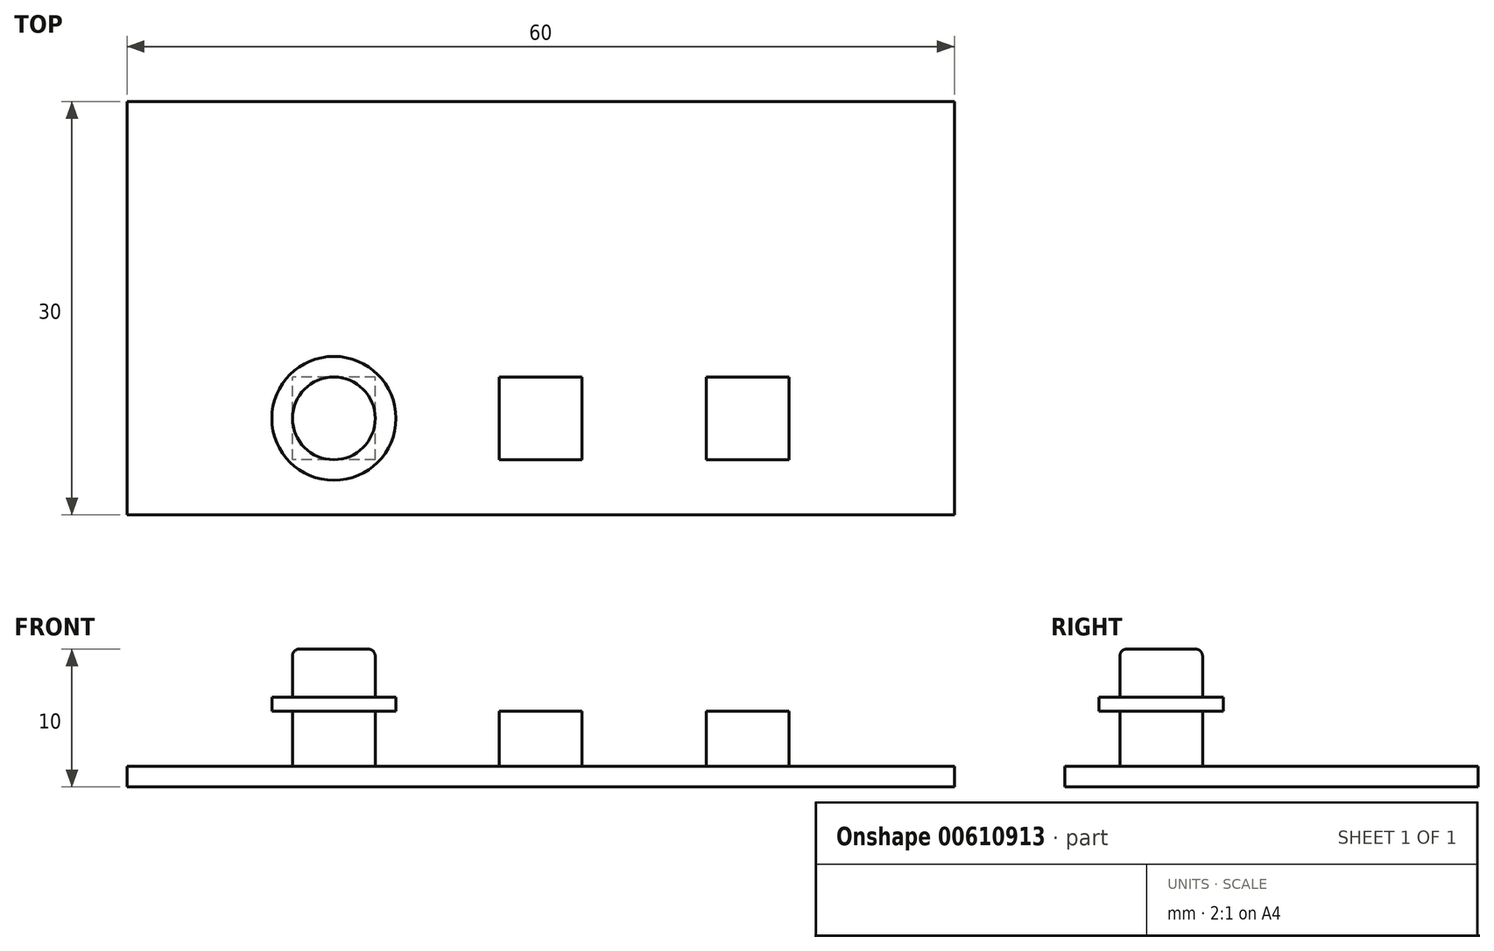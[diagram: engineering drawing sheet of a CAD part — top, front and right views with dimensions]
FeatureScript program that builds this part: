
annotation { "Feature Type Name" : "Feature", "Feature Type Description" : "" }
export const myFeature = defineFeature(function(context is Context, id is Id, definition is map)
    precondition{}
    {
        {
            var Q0;
            Q0=qCreatedBy(makeId("Top.planeOp"),FACE);
            var sketch = newSketch(context, id + "F0", { "sketchPlane" : qUnion([Q0])});
            skLineSegment(sketch, "E0.bottom", {"start": v(30, -15) * mm, "end": v(-30, -15) * mm});
            skLineSegment(sketch, "E0.top", {"start": v(30, 15) * mm, "end": v(-30, 15) * mm});
            skLineSegment(sketch, "E0.left", {"start": v(30, -15) * mm, "end": v(30, 15) * mm});
            skLineSegment(sketch, "E0.right", {"start": v(-30, -15) * mm, "end": v(-30, 15) * mm});
            skPoint(sketch, "E0.middle", {"position": v(0, 0) * mm});
            skSolve(sketch);
        }
        {
            var Q0;
            Q0=makeQuery(id+"F0.imprint","IMPRINT",FACE,{"disambiguationData":[TD([[makeQuery(id+"F0.imprint","IMPRINT",EDGE,{"derivedFrom":sQuery(id+"F0.wireOp",EDGE,"E0.bottom")}),-1.0]])]});
            extrude(context, id + "F1", {"entities" : qUnion([Q0]), "depth" : 1.5 * mm, "offsetDistance" : 25 * mm});
        }
        {
            var Q0;
            Q0=makeQuery(id+"F1.opExtrude","CAP_FACE",FACE,{"disambiguationData":[OSD([sQuery(id+"F0.wireOp",EDGE,"E0.bottom"),sQuery(id+"F0.wireOp",EDGE,"E0.top"),sQuery(id+"F0.wireOp",EDGE,"E0.left"),sQuery(id+"F0.wireOp",EDGE,"E0.right")])],"isStart":false});
            var sketch = newSketch(context, id + "F2", { "sketchPlane" : qUnion([Q0])});
            skLineSegment(sketch, "E1.bottom", {"start": v(-12, -11) * mm, "end": v(-18, -11) * mm});
            skLineSegment(sketch, "E1.top", {"start": v(-12, -5) * mm, "end": v(-18, -5) * mm});
            skLineSegment(sketch, "E1.left", {"start": v(-12, -11) * mm, "end": v(-12, -5) * mm});
            skLineSegment(sketch, "E1.right", {"start": v(-18, -11) * mm, "end": v(-18, -5) * mm});
            skPoint(sketch, "E1.middle", {"position": v(-15, -8) * mm});
            skLineSegment(sketch, "E2.1.0.0", {"start": v(3, -11) * mm, "end": v(-3, -11) * mm});
            skLineSegment(sketch, "E2.1.0.1", {"start": v(-3, -11) * mm, "end": v(-3, -5) * mm});
            skLineSegment(sketch, "E2.1.0.2", {"start": v(3, -5) * mm, "end": v(-3, -5) * mm});
            skLineSegment(sketch, "E2.1.0.3", {"start": v(3, -11) * mm, "end": v(3, -5) * mm});
            skLineSegment(sketch, "E2.2.0.0", {"start": v(18, -11) * mm, "end": v(12, -11) * mm});
            skLineSegment(sketch, "E2.2.0.1", {"start": v(12, -11) * mm, "end": v(12, -5) * mm});
            skLineSegment(sketch, "E2.2.0.2", {"start": v(18, -5) * mm, "end": v(12, -5) * mm});
            skLineSegment(sketch, "E2.2.0.3", {"start": v(18, -11) * mm, "end": v(18, -5) * mm});
            skLineSegment(sketch, "E2.direction1", {"start": v(-18, -11) * mm, "end": v(-3, -11) * mm, "construction": true});
            skSolve(sketch);
        }
        {
            var Q0;
            Q0 = qSketchRegion(id + "F2", true);
            extrude(context, id + "F3", {"entities" : qUnion([Q0]), "operationType" : NewBodyOperationType.ADD, "depth" : 4 * mm, "offsetDistance" : 25 * mm});
        }
        {
            var Q0;
            Q0=makeQuery(id+"F3.opExtrude","CAP_FACE",FACE,{"disambiguationData":[OSD([sQuery(id+"F2.wireOp",EDGE,"E1.bottom"),sQuery(id+"F2.wireOp",EDGE,"E1.top"),sQuery(id+"F2.wireOp",EDGE,"E1.left"),sQuery(id+"F2.wireOp",EDGE,"E1.right")])],"isStart":false});
            var sketch = newSketch(context, id + "F4", { "sketchPlane" : qUnion([Q0])});
            skCircle(sketch, "E3", {"center": v(-15, -8) * mm, "radius": 4.5 * mm});
            skPoint(sketch, "E3.centerSnap0", {"position": v(-18, -8) * mm});
            skPoint(sketch, "E3.centerSnap1", {"position": v(-15, -5) * mm});
            skSolve(sketch);
        }
        {
            var Q0;
            Q0 = qSketchRegion(id + "F4", true);
            extrude(context, id + "F5", {"entities" : qUnion([Q0]), "depth" : 1 * mm, "offsetDistance" : 25 * mm});
        }
        {
            var Q0;
            Q0=makeQuery(id+"F5.opExtrude","CAP_FACE",FACE,{"disambiguationData":[OSD([sQuery(id+"F4.wireOp",EDGE,"E3")])],"isStart":false});
            var sketch = newSketch(context, id + "F6", { "sketchPlane" : qUnion([Q0])});
            skCircle(sketch, "E4", {"center": v(-15, -8) * mm, "radius": 3 * mm});
            skSolve(sketch);
        }
        {
            var Q0;
            Q0 = qSketchRegion(id + "F6", true);
            extrude(context, id + "F7", {"entities" : qUnion([Q0]), "operationType" : NewBodyOperationType.ADD, "depth" : 3.5 * mm, "offsetDistance" : 25 * mm});
        }
        {
            var Q0;
            Q0=makeQuery(id+"F7.opExtrude","CAP_EDGE",EDGE,{"disambiguationData":[OSD([sQuery(id+"F6.wireOp",EDGE,"E4")])],"isStart":false});
            fillet(context, id + "F8", {"entities" : qUnion([Q0]), "radius" : 0.5 * mm, "tangentPropagation" : true, "allowEdgeOverflow" : false});
        }
    });
